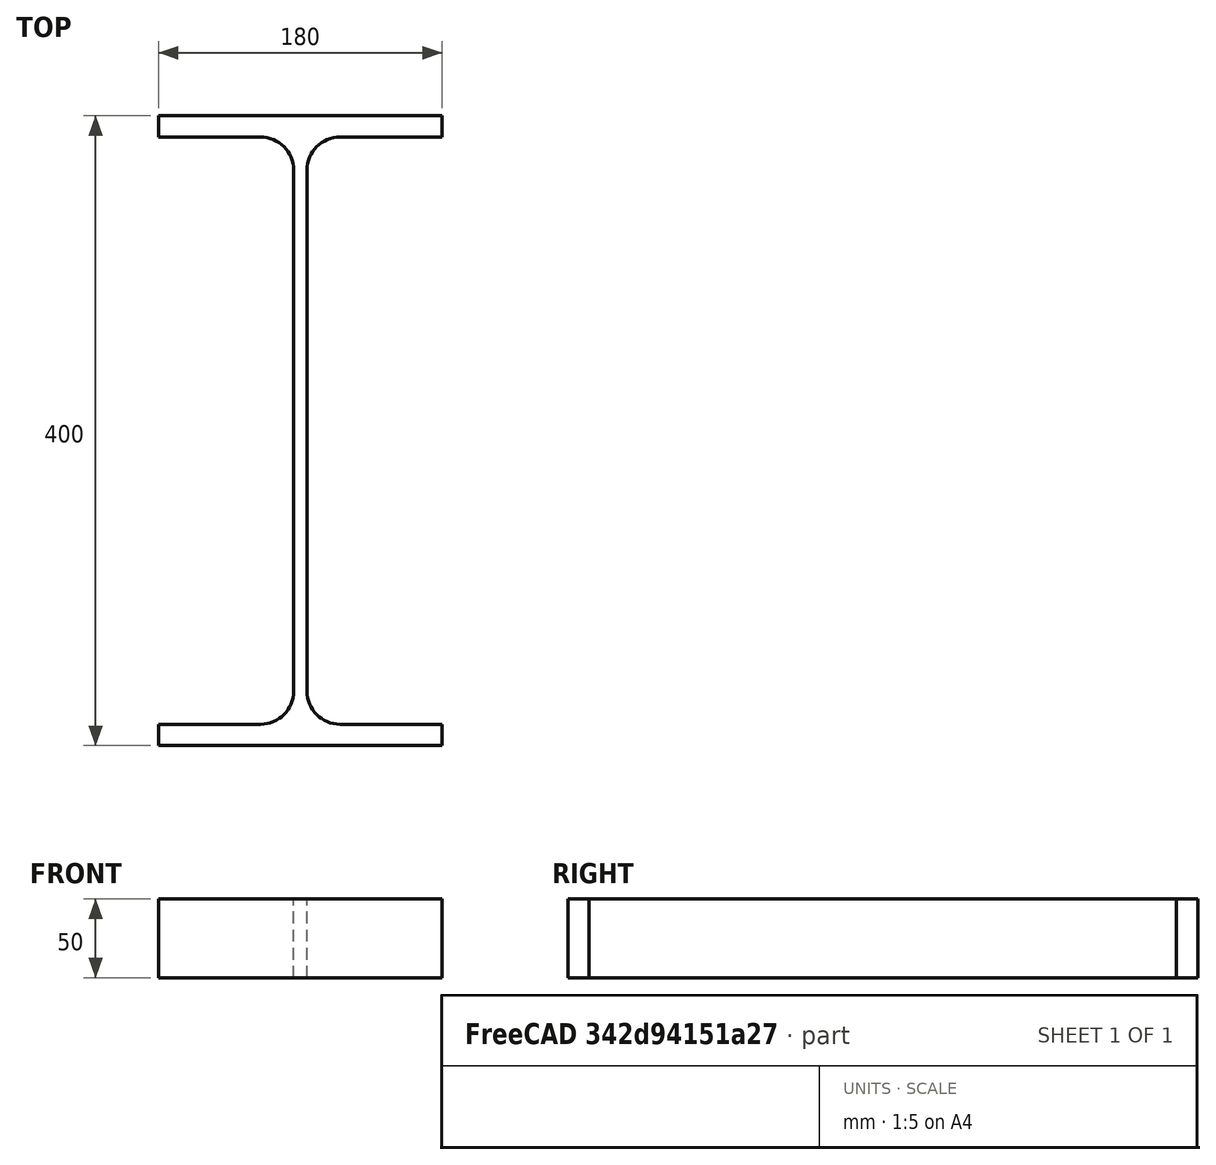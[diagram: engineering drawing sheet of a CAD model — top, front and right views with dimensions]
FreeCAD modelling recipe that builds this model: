
FCSTD DOCUMENT  (FreeCAD 0.15R4671 (Git))
Label: IPE-Profile 400 DIN1025-5 S235JR
License: All rights reserved
LicenseURL: http://en.wikipedia.org/wiki/All_rights_reserved
objects: Sketcher::SketchObject×1, Part::Extrusion×1
note: 2 computed .brp shape members not serialized (recipe doc carries the construction recipe); baked Part::Feature solids carry a one-line shape summary decoded from their .brp

FEATURE [Sketcher::SketchObject] Sketch
  sketch-geometry (16):
    g0: LineSegment StartX=4.3 StartY=-165.5 StartZ=0 EndX=4.3 EndY=165.5 EndZ=0
    g1: LineSegment StartX=25.3 StartY=186.5 StartZ=0 EndX=90 EndY=186.5 EndZ=0
    g2: LineSegment StartX=90 StartY=186.5 StartZ=0 EndX=90 EndY=200 EndZ=0
    g3: LineSegment StartX=90 StartY=200 StartZ=0 EndX=-90 EndY=200 EndZ=0
    g4: LineSegment StartX=-90 StartY=200 StartZ=0 EndX=-90 EndY=186.5 EndZ=0
    g5: LineSegment StartX=-90 StartY=186.5 StartZ=0 EndX=-25.3 EndY=186.5 EndZ=0
    g6: LineSegment StartX=-4.3 StartY=165.5 StartZ=0 EndX=-4.3 EndY=-165.5 EndZ=0
    g7: LineSegment StartX=-25.3 StartY=-186.5 StartZ=0 EndX=-90 EndY=-186.5 EndZ=0
    g8: LineSegment StartX=-90 StartY=-186.5 StartZ=0 EndX=-90 EndY=-200 EndZ=0
    g9: LineSegment StartX=-90 StartY=-200 StartZ=0 EndX=90 EndY=-200 EndZ=0
    g10: LineSegment StartX=90 StartY=-200 StartZ=0 EndX=90 EndY=-186.5 EndZ=0
    g11: LineSegment StartX=90 StartY=-186.5 StartZ=0 EndX=25.3 EndY=-186.5 EndZ=0
    g12: ArcOfCircle CenterX=25.3 CenterY=165.5 CenterZ=0 NormalX=0 NormalY=0 NormalZ=1 Radius=21 StartAngle=1.5708 EndAngle=3.14159
    g13: ArcOfCircle CenterX=25.3 CenterY=-165.5 CenterZ=0 NormalX=0 NormalY=0 NormalZ=1 Radius=21 StartAngle=3.14159 EndAngle=4.71239
    g14: ArcOfCircle CenterX=-25.3 CenterY=165.5 CenterZ=0 NormalX=0 NormalY=0 NormalZ=1 Radius=21 StartAngle=0 EndAngle=1.5708
    g15: ArcOfCircle CenterX=-25.3 CenterY=-165.5 CenterZ=0 NormalX=0 NormalY=0 NormalZ=1 Radius=21 StartAngle=4.71239 EndAngle=6.28319
  constraints (42):
    c: Vertical(g0)
    c: Coincident(g2,g1)
    c: Vertical(g2)
    c: Coincident(g3,g2)
    c: Coincident(g4,g3)
    c: Vertical(g4)
    c: Coincident(g5,g4)
    c: Horizontal(g5)
    c: Vertical(g6)
    c: Horizontal(g7)
    c: Coincident(g8,g7)
    c: Vertical(g8)
    c: Coincident(g9,g8)
    c: Horizontal(g9)
    c: Coincident(g10,g9)
    c: Vertical(g10)
    c: Coincident(g11,g10)
    c: Horizontal(g11)
    c: Tangent(g1,g12) = 1.5708
    c: Tangent(g0,g12) = 1.5708
    c: Tangent(g0,g13) = 1.5708
    c: Tangent(g11,g13) = 1.5708
    c: Tangent(g5,g14) = 1.5708
    c: Tangent(g6,g14) = 1.5708
    c: Tangent(g6,g15) = 1.5708
    c: Tangent(g7,g15) = 1.5708
    c: Equal(g3,g9)
    c: Equal(g2,g4)
    c: Equal(g4,g8)
    c: Equal(g8,g10)
    c: Equal(g12,g14)
    c: Equal(g14,g15)
    c: Equal(g15,g13)
    c: Symmetric(g2,g3,g-2)
    c: Symmetric(g9,g8,g-2)
    c: Symmetric(g0,g6,g-2)
    c: Symmetric(g2,g9,g-1)
    c: DistanceY(g2,g9) = -400
    c: DistanceX(g3) = -180
    c: DistanceX(g0,g6) = -8.6
    c: DistanceY(g2) = 13.5
    c: Radius(g12) = 21
FEATURE [Part::Extrusion] Extrude  label="IPE-Profile 400 DIN1025-5 S235JR"
  Base = -> Sketch
  Dir = (0,0,50)
  Solid = true
